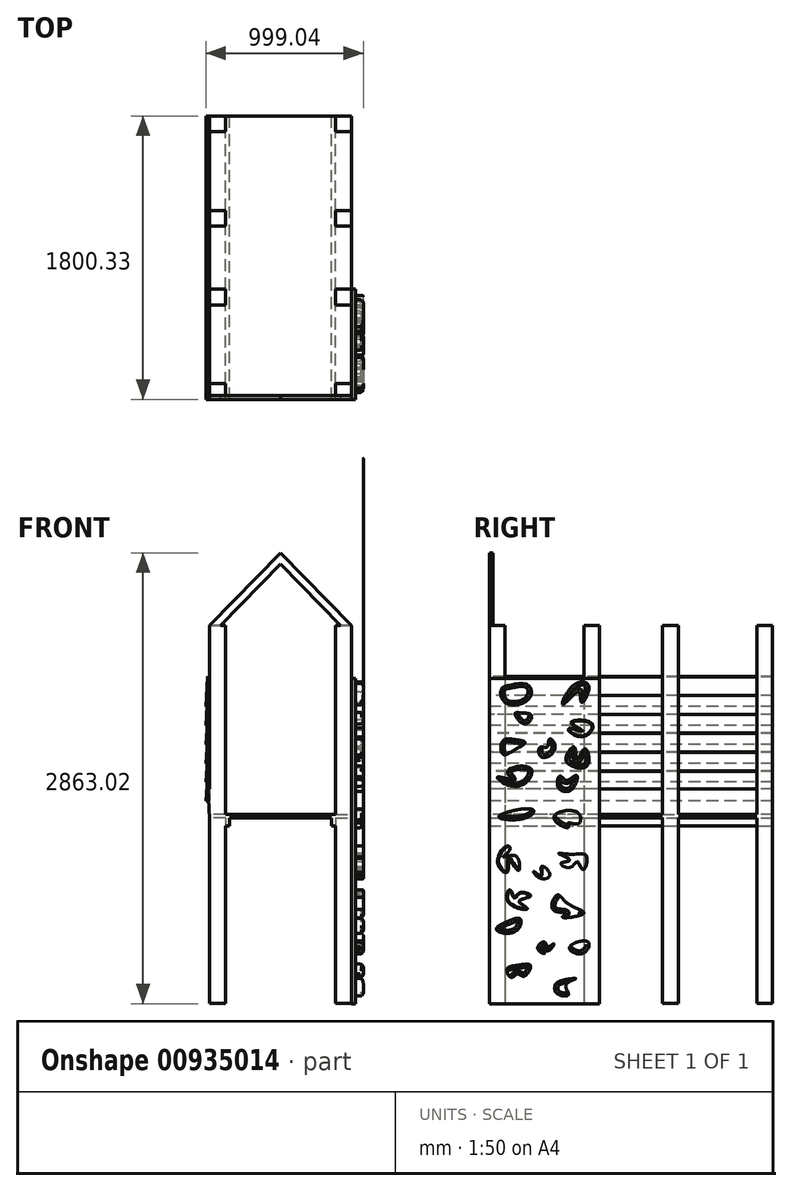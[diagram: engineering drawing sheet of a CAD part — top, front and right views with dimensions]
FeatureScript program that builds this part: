
annotation { "Feature Type Name" : "Feature", "Feature Type Description" : "" }
export const myFeature = defineFeature(function(context is Context, id is Id, definition is map)
    precondition{}
    {
        {
            var Q0;
            Q0=qCreatedBy(makeId("Top.planeOp"),FACE);
            var sketch = newSketch(context, id + "F0", { "sketchPlane" : qUnion([Q0])});
            skLineSegment(sketch, "E0.bottom", {"start": v(450, 900) * mm, "end": v(-450, 900) * mm});
            skLineSegment(sketch, "E0.top", {"start": v(450, -900) * mm, "end": v(-450, -900) * mm});
            skLineSegment(sketch, "E0.left", {"start": v(450, 900) * mm, "end": v(450, -900) * mm});
            skLineSegment(sketch, "E0.right", {"start": v(-450, 900) * mm, "end": v(-450, -900) * mm});
            skPoint(sketch, "E0.middle", {"position": v(0, 0) * mm});
            skSolve(sketch);
        }
        {
            var Q0;
            Q0=makeQuery(id+"F0.imprint","IMPRINT",FACE,{"disambiguationData":[TD([[makeQuery(id+"F0.imprint","IMPRINT",EDGE,{"derivedFrom":sQuery(id+"F0.wireOp",EDGE,"E0.bottom")}),1.0]])]});
            extrude(context, id + "F1", {"entities" : qUnion([Q0]), "depth" : 22 * mm, "offsetDistance" : 25 * mm});
        }
        {
            var Q0;
            Q0=makeQuery(id+"F1.opExtrude","CAP_FACE",FACE,{"disambiguationData":[OSD([sQuery(id+"F0.wireOp",EDGE,"E0.bottom"),sQuery(id+"F0.wireOp",EDGE,"E0.top"),sQuery(id+"F0.wireOp",EDGE,"E0.left"),sQuery(id+"F0.wireOp",EDGE,"E0.right")])],"isStart":false});
            var sketch = newSketch(context, id + "F2", { "sketchPlane" : qUnion([Q0])});
            skLineSegment(sketch, "E1.bottom", {"start": v(-450, 900) * mm, "end": v(-350, 900) * mm});
            skLineSegment(sketch, "E1.top", {"start": v(-450, 800) * mm, "end": v(-350, 800) * mm});
            skLineSegment(sketch, "E1.left", {"start": v(-450, 900) * mm, "end": v(-450, 800) * mm});
            skLineSegment(sketch, "E1.right", {"start": v(-350, 900) * mm, "end": v(-350, 800) * mm});
            skLineSegment(sketch, "E2.bottom", {"start": v(350, 800) * mm, "end": v(450, 800) * mm});
            skLineSegment(sketch, "E2.top", {"start": v(350, 900) * mm, "end": v(450, 900) * mm});
            skLineSegment(sketch, "E2.left", {"start": v(350, 800) * mm, "end": v(350, 900) * mm});
            skLineSegment(sketch, "E2.right", {"start": v(450, 800) * mm, "end": v(450, 900) * mm});
            skLineSegment(sketch, "E3.bottom", {"start": v(-450, -900) * mm, "end": v(-350, -900) * mm});
            skLineSegment(sketch, "E3.top", {"start": v(-450, -800) * mm, "end": v(-350, -800) * mm});
            skLineSegment(sketch, "E3.left", {"start": v(-450, -900) * mm, "end": v(-450, -800) * mm});
            skLineSegment(sketch, "E3.right", {"start": v(-350, -900) * mm, "end": v(-350, -800) * mm});
            skLineSegment(sketch, "E4.bottom", {"start": v(450, -900) * mm, "end": v(350, -900) * mm});
            skLineSegment(sketch, "E4.top", {"start": v(450, -800) * mm, "end": v(350, -800) * mm});
            skLineSegment(sketch, "E4.left", {"start": v(450, -900) * mm, "end": v(450, -800) * mm});
            skLineSegment(sketch, "E4.right", {"start": v(350, -900) * mm, "end": v(350, -800) * mm});
            skLineSegment(sketch, "E5.bottom", {"start": v(350, -300) * mm, "end": v(450, -300) * mm});
            skLineSegment(sketch, "E5.top", {"start": v(350, -200) * mm, "end": v(450, -200) * mm});
            skLineSegment(sketch, "E5.left", {"start": v(350, -300) * mm, "end": v(350, -200) * mm});
            skLineSegment(sketch, "E5.right", {"start": v(450, -300) * mm, "end": v(450, -200) * mm});
            skLineSegment(sketch, "E6.bottom", {"start": v(450, 300) * mm, "end": v(350, 300) * mm});
            skLineSegment(sketch, "E6.top", {"start": v(450, 200) * mm, "end": v(350, 200) * mm});
            skLineSegment(sketch, "E6.left", {"start": v(450, 300) * mm, "end": v(450, 200) * mm});
            skLineSegment(sketch, "E6.right", {"start": v(350, 300) * mm, "end": v(350, 200) * mm});
            skLineSegment(sketch, "E7.bottom", {"start": v(-450, 300) * mm, "end": v(-350, 300) * mm});
            skLineSegment(sketch, "E7.top", {"start": v(-450, 200) * mm, "end": v(-350, 200) * mm});
            skLineSegment(sketch, "E7.left", {"start": v(-450, 300) * mm, "end": v(-450, 200) * mm});
            skLineSegment(sketch, "E7.right", {"start": v(-350, 300) * mm, "end": v(-350, 200) * mm});
            skLineSegment(sketch, "E8.bottom", {"start": v(-450, -300) * mm, "end": v(-350, -300) * mm});
            skLineSegment(sketch, "E8.top", {"start": v(-450, -200) * mm, "end": v(-350, -200) * mm});
            skLineSegment(sketch, "E8.left", {"start": v(-450, -300) * mm, "end": v(-450, -200) * mm});
            skLineSegment(sketch, "E8.right", {"start": v(-350, -300) * mm, "end": v(-350, -200) * mm});
            skSolve(sketch);
        }
        {
            var Q0;
            Q0 = qSketchRegion(id + "F2", true);
            extrude(context, id + "F3", {"entities" : qUnion([Q0]), "operationType" : NewBodyOperationType.ADD, "depth" : 1200 * mm, "offsetDistance" : 25 * mm, "hasSecondDirection" : true, "secondDirectionOppositeDirection" : true, "secondDirectionDepth" : 1200 * mm});
        }
        {
            var Q0;
            Q0=makeQuery(id+"F1.opExtrude","CAP_FACE",FACE,{"disambiguationData":[OSD([sQuery(id+"F0.wireOp",EDGE,"E0.bottom"),sQuery(id+"F0.wireOp",EDGE,"E0.top"),sQuery(id+"F0.wireOp",EDGE,"E0.left"),sQuery(id+"F0.wireOp",EDGE,"E0.right")])],"isStart":true});
            var sketch = newSketch(context, id + "F4", { "sketchPlane" : qUnion([Q0])});
            skLineSegment(sketch, "E9.bottom", {"start": v(-350, 900) * mm, "end": v(-325, 900) * mm});
            skLineSegment(sketch, "E9.top", {"start": v(-350, -900) * mm, "end": v(-325, -900) * mm});
            skLineSegment(sketch, "E9.left", {"start": v(-350, 900) * mm, "end": v(-350, -900) * mm});
            skLineSegment(sketch, "E9.right", {"start": v(-325, 900) * mm, "end": v(-325, -900) * mm});
            skLineSegment(sketch, "E10.bottom", {"start": v(350, 900) * mm, "end": v(325, 900) * mm});
            skLineSegment(sketch, "E10.top", {"start": v(350, -900) * mm, "end": v(325, -900) * mm});
            skLineSegment(sketch, "E10.left", {"start": v(350, 900) * mm, "end": v(350, -900) * mm});
            skLineSegment(sketch, "E10.right", {"start": v(325, 900) * mm, "end": v(325, -900) * mm});
            skSolve(sketch);
        }
        {
            var Q0;
            Q0 = qSketchRegion(id + "F4", true);
            extrude(context, id + "F5", {"entities" : qUnion([Q0]), "operationType" : NewBodyOperationType.ADD, "depth" : 50 * mm, "offsetDistance" : 25 * mm});
        }
        {
            var Q0;
            Q0=makeQuery(id+"F5.boolean.opBoolean","MERGE",FACE,{"derivedFrom":[makeQuery(id+"F3.boolean.opBoolean","MERGE",FACE,{"derivedFrom":[makeQuery(id+"F1.opExtrude","SWEPT_FACE",FACE,{"disambiguationData":[OSD([sQuery(id+"F0.wireOp",EDGE,"E0.top")])]}),makeQuery(id+"F3.opExtrude","SWEPT_FACE",FACE,{"disambiguationData":[OSD([sQuery(id+"F2.wireOp",EDGE,"E3.bottom")])]}),makeQuery(id+"F3.opExtrude","SWEPT_FACE",FACE,{"disambiguationData":[OSD([sQuery(id+"F2.wireOp",EDGE,"E4.bottom")])]})]}),makeQuery(id+"F5.opExtrude","SWEPT_FACE",FACE,{"disambiguationData":[OSD([sQuery(id+"F4.wireOp",EDGE,"E9.bottom")])]}),makeQuery(id+"F5.opExtrude","SWEPT_FACE",FACE,{"disambiguationData":[OSD([sQuery(id+"F4.wireOp",EDGE,"E10.bottom")])]})]});
            var sketch = newSketch(context, id + "F6", { "sketchPlane" : qUnion([Q0])});
            skLineSegment(sketch, "E11", {"start": v(-450, 185.3) * mm, "end": v(-450, -4.7) * mm});
            skLineSegment(sketch, "E12", {"start": v(-450, -4.7) * mm, "end": v(-453, -4.7) * mm});
            skLineSegment(sketch, "E13", {"start": v(-453, -4.7) * mm, "end": v(-462, 184.95) * mm});
            skLineSegment(sketch, "E14", {"start": v(-462, 184.95) * mm, "end": v(-450, 185.3) * mm});
            skSolve(sketch);
        }
        {
            var Q0;
            Q0 = qSketchRegion(id + "F6", true);
            extrude(context, id + "F7", {"entities" : qUnion([Q0]), "operationType" : NewBodyOperationType.ADD, "oppositeDirection" : true, "depth" : 1800 * mm, "offsetDistance" : 25 * mm});
        }
        {
            var Q0;
            Q0=makeQuery(id+"F7.boolean.opBoolean","MERGE",FACE,{"derivedFrom":[makeQuery(id+"F5.boolean.opBoolean","MERGE",FACE,{"derivedFrom":[makeQuery(id+"F3.boolean.opBoolean","MERGE",FACE,{"derivedFrom":[makeQuery(id+"F1.opExtrude","SWEPT_FACE",FACE,{"disambiguationData":[OSD([sQuery(id+"F0.wireOp",EDGE,"E0.top")])]}),makeQuery(id+"F3.opExtrude","SWEPT_FACE",FACE,{"disambiguationData":[OSD([sQuery(id+"F2.wireOp",EDGE,"E3.bottom")])]}),makeQuery(id+"F3.opExtrude","SWEPT_FACE",FACE,{"disambiguationData":[OSD([sQuery(id+"F2.wireOp",EDGE,"E4.bottom")])]})]}),makeQuery(id+"F5.opExtrude","SWEPT_FACE",FACE,{"disambiguationData":[OSD([sQuery(id+"F4.wireOp",EDGE,"E9.bottom")])]}),makeQuery(id+"F5.opExtrude","SWEPT_FACE",FACE,{"disambiguationData":[OSD([sQuery(id+"F4.wireOp",EDGE,"E10.bottom")])]})]}),makeQuery(id+"F7.opExtrude","CAP_FACE",FACE,{"disambiguationData":[OSD([sQuery(id+"F6.wireOp",EDGE,"E11"),sQuery(id+"F6.wireOp",EDGE,"E12"),sQuery(id+"F6.wireOp",EDGE,"E13"),sQuery(id+"F6.wireOp",EDGE,"E14")])],"isStart":true})]});
            var sketch = newSketch(context, id + "F8", { "sketchPlane" : qUnion([Q0])});
            skLineSegment(sketch, "E15", {"start": v(-450, 295.94) * mm, "end": v(-470.4, 107.04) * mm});
            skLineSegment(sketch, "E16", {"start": v(-470.4, 107.04) * mm, "end": v(-473.4, 107.04) * mm});
            skLineSegment(sketch, "E17", {"start": v(-473.4, 107.04) * mm, "end": v(-461.86, 297.77) * mm});
            skLineSegment(sketch, "E18", {"start": v(-461.86, 297.77) * mm, "end": v(-450, 295.94) * mm});
            skLineSegment(sketch, "E19.0.1.0", {"start": v(-470.53, 227.05) * mm, "end": v(-473.53, 227.05) * mm});
            skLineSegment(sketch, "E19.0.1.1", {"start": v(-461.99, 417.78) * mm, "end": v(-450.13, 415.95) * mm});
            skLineSegment(sketch, "E19.0.1.2", {"start": v(-450.13, 415.95) * mm, "end": v(-470.53, 227.05) * mm});
            skLineSegment(sketch, "E19.0.1.3", {"start": v(-473.53, 227.05) * mm, "end": v(-461.99, 417.78) * mm});
            skLineSegment(sketch, "E19.0.2.0", {"start": v(-470.65, 347.06) * mm, "end": v(-473.65, 347.06) * mm});
            skLineSegment(sketch, "E19.0.2.1", {"start": v(-462.12, 537.8) * mm, "end": v(-450.26, 535.96) * mm});
            skLineSegment(sketch, "E19.0.2.2", {"start": v(-450.26, 535.96) * mm, "end": v(-470.65, 347.06) * mm});
            skLineSegment(sketch, "E19.0.2.3", {"start": v(-473.65, 347.06) * mm, "end": v(-462.12, 537.8) * mm});
            skLineSegment(sketch, "E19.0.3.0", {"start": v(-470.78, 467.07) * mm, "end": v(-473.78, 467.07) * mm});
            skLineSegment(sketch, "E19.0.3.1", {"start": v(-462.24, 657.8) * mm, "end": v(-450.38, 655.97) * mm});
            skLineSegment(sketch, "E19.0.3.2", {"start": v(-450.38, 655.97) * mm, "end": v(-470.78, 467.07) * mm});
            skLineSegment(sketch, "E19.0.3.3", {"start": v(-473.78, 467.07) * mm, "end": v(-462.24, 657.8) * mm});
            skLineSegment(sketch, "E19.0.4.0", {"start": v(-470.91, 587.08) * mm, "end": v(-473.91, 587.08) * mm});
            skLineSegment(sketch, "E19.0.4.1", {"start": v(-462.37, 777.81) * mm, "end": v(-450.51, 775.98) * mm});
            skLineSegment(sketch, "E19.0.4.2", {"start": v(-450.51, 775.98) * mm, "end": v(-470.91, 587.08) * mm});
            skLineSegment(sketch, "E19.0.4.3", {"start": v(-473.91, 587.08) * mm, "end": v(-462.37, 777.81) * mm});
            skLineSegment(sketch, "E19.0.5.0", {"start": v(-471.04, 707.1) * mm, "end": v(-474.04, 707.1) * mm});
            skLineSegment(sketch, "E19.0.5.1", {"start": v(-462.5, 897.82) * mm, "end": v(-450.64, 896) * mm});
            skLineSegment(sketch, "E19.0.5.2", {"start": v(-450.64, 896) * mm, "end": v(-471.04, 707.1) * mm});
            skLineSegment(sketch, "E19.0.5.3", {"start": v(-474.04, 707.1) * mm, "end": v(-462.5, 897.82) * mm});
            skLineSegment(sketch, "E19.direction1", {"start": v(-461.86, 297.77) * mm, "end": v(-436.86, 297.77) * mm, "construction": true});
            skLineSegment(sketch, "E19.direction2", {"start": v(-461.86, 297.77) * mm, "end": v(-461.99, 417.78) * mm, "construction": true});
            skSolve(sketch);
        }
        {
            var Q0;
            Q0=makeQuery(id+"F8.imprint","IMPRINT",FACE,{"disambiguationData":[TD([[makeQuery(id+"F8.imprint","IMPRINT",EDGE,{"derivedFrom":sQuery(id+"F8.wireOp",EDGE,"E19.0.1.0")}),-1.0]])]});
            var Q1;
            Q1=makeQuery(id+"F8.imprint","IMPRINT",FACE,{"disambiguationData":[TD([[makeQuery(id+"F8.imprint","IMPRINT",EDGE,{"derivedFrom":sQuery(id+"F8.wireOp",EDGE,"E19.0.2.0")}),-1.0]])]});
            var Q2;
            Q2=makeQuery(id+"F8.imprint","IMPRINT",FACE,{"disambiguationData":[TD([[makeQuery(id+"F8.imprint","IMPRINT",EDGE,{"derivedFrom":sQuery(id+"F8.wireOp",EDGE,"E19.0.3.0")}),-1.0]])]});
            var Q3;
            Q3=makeQuery(id+"F8.imprint","IMPRINT",FACE,{"disambiguationData":[TD([[makeQuery(id+"F8.imprint","IMPRINT",EDGE,{"derivedFrom":sQuery(id+"F8.wireOp",EDGE,"E19.0.4.0")}),-1.0]])]});
            var Q4;
            Q4=makeQuery(id+"F8.imprint","IMPRINT",FACE,{"disambiguationData":[TD([[makeQuery(id+"F8.imprint","IMPRINT",EDGE,{"derivedFrom":sQuery(id+"F8.wireOp",EDGE,"E19.0.5.0")}),-1.0]])]});
            extrude(context, id + "F9", {"entities" : qUnion([Q0, Q1, Q2, Q3, Q4]), "oppositeDirection" : true, "depth" : 1800 * mm, "offsetDistance" : 25 * mm});
        }
        {
            var Q0;
            {var subQ0=sQuery(id+"F8.wireOp",EDGE,"E16");Q0=makeQuery(id+"F8.imprint","IMPRINT",FACE,{"disambiguationData":[TD([[makeQuery(id+"F8.imprint","IMPRINT",EDGE,{"derivedFrom":subQ0}),-1.0]])]});}
            extrude(context, id + "F10", {"entities" : qUnion([Q0]), "oppositeDirection" : true, "depth" : 1800 * mm, "offsetDistance" : 25 * mm});
        }
        {
            var Q0;
            Q0=makeQuery(id+"F7.boolean.opBoolean","MERGE",FACE,{"derivedFrom":[makeQuery(id+"F5.boolean.opBoolean","MERGE",FACE,{"derivedFrom":[makeQuery(id+"F3.boolean.opBoolean","MERGE",FACE,{"derivedFrom":[makeQuery(id+"F1.opExtrude","SWEPT_FACE",FACE,{"disambiguationData":[OSD([sQuery(id+"F0.wireOp",EDGE,"E0.bottom")])]}),makeQuery(id+"F3.opExtrude","SWEPT_FACE",FACE,{"disambiguationData":[OSD([sQuery(id+"F2.wireOp",EDGE,"E1.bottom")])]}),makeQuery(id+"F3.opExtrude","SWEPT_FACE",FACE,{"disambiguationData":[OSD([sQuery(id+"F2.wireOp",EDGE,"E2.top")])]})]}),makeQuery(id+"F5.opExtrude","SWEPT_FACE",FACE,{"disambiguationData":[OSD([sQuery(id+"F4.wireOp",EDGE,"E9.top")])]}),makeQuery(id+"F5.opExtrude","SWEPT_FACE",FACE,{"disambiguationData":[OSD([sQuery(id+"F4.wireOp",EDGE,"E10.top")])]})]}),makeQuery(id+"F7.opExtrude","CAP_FACE",FACE,{"disambiguationData":[OSD([sQuery(id+"F6.wireOp",EDGE,"E11"),sQuery(id+"F6.wireOp",EDGE,"E12"),sQuery(id+"F6.wireOp",EDGE,"E13"),sQuery(id+"F6.wireOp",EDGE,"E14")])],"isStart":false})]});
            cPlane(context, id + "F11", {"entities" : qUnion([Q0]), "cplaneType" : CPlaneType.OFFSET, "offset" : 300 * mm, "oppositeDirection" : true, "width" : 150 * mm, "height" : 150 * mm});
        }
        {
            var Q0;
            Q0=qCreatedBy(id+"F11.planeOp",FACE);
            var sketch = newSketch(context, id + "F12", { "sketchPlane" : qUnion([Q0])});
            skFitSpline(sketch, "E20", {"points": [v(-446.84, 20.94) * mm, v(-1018.85, -218.36) * mm, v(-1616.22, -815.28) * mm, v(-2211.53, -1175.8) * mm], "startDerivative": vector(-3689.56, -4.26) * mm, "endDerivative": vector(-1535.93, 0) * mm});
            skLineSegment(sketch, "E21", {"start": v(-448.7, -1175.8) * mm, "end": v(-2388.55, -1175.8) * mm, "construction": true});
            skSolve(sketch);
        }
        {
            var Q0;
            Q0=makeQuery(id+"F3.boolean.opBoolean","MERGE",FACE,{"derivedFrom":[makeQuery(id+"F1.opExtrude","SWEPT_FACE",FACE,{"disambiguationData":[OSD([sQuery(id+"F0.wireOp",EDGE,"E0.left")])]}),makeQuery(id+"F3.opExtrude","SWEPT_FACE",FACE,{"disambiguationData":[OSD([sQuery(id+"F2.wireOp",EDGE,"E2.right")])]}),makeQuery(id+"F3.opExtrude","SWEPT_FACE",FACE,{"disambiguationData":[OSD([sQuery(id+"F2.wireOp",EDGE,"E4.left")])]}),makeQuery(id+"F3.opExtrude","SWEPT_FACE",FACE,{"disambiguationData":[OSD([sQuery(id+"F2.wireOp",EDGE,"E5.right")])]}),makeQuery(id+"F3.opExtrude","SWEPT_FACE",FACE,{"disambiguationData":[OSD([sQuery(id+"F2.wireOp",EDGE,"E6.left")])]})]});
            var sketch = newSketch(context, id + "F13", { "sketchPlane" : qUnion([Q0])});
            skLineSegment(sketch, "E22.bottom", {"start": v(300, 70.69) * mm, "end": v(332.87, 70.69) * mm});
            skLineSegment(sketch, "E22.top", {"start": v(300, 0) * mm, "end": v(800, 0) * mm});
            skLineSegment(sketch, "E22.left", {"start": v(300, 70.69) * mm, "end": v(300, 0) * mm});
            skLineSegment(sketch, "E22.right", {"start": v(800, 70.69) * mm, "end": v(800, 0) * mm});
            skLineSegment(sketch, "E23.top", {"start": v(332.87, 22) * mm, "end": v(769.2, 22) * mm});
            skLineSegment(sketch, "E23.left", {"start": v(332.87, 70.69) * mm, "end": v(332.87, 22) * mm});
            skLineSegment(sketch, "E23.right", {"start": v(769.2, 70.69) * mm, "end": v(769.2, 22) * mm});
            skLineSegment(sketch, "E24.trimOffspring", {"start": v(769.2, 70.69) * mm, "end": v(800, 70.69) * mm});
            skSolve(sketch);
        }
        {
            var Q0;
            Q0 = qSketchRegion(id + "F13", true);
            var Q1;
            Q1 = qBodyType(qCreatedBy(id + "F13" ,EDGE), BodyType.WIRE);
            var Q2;
            Q2 = qBodyType(qCreatedBy(id + "F12" ,EDGE), BodyType.WIRE);
            sweep(context, id + "F14", {"bodyType" : ToolBodyType.SURFACE, "operationType" : NewBodyOperationType.ADD, "profiles" : qUnion([Q0]), "surfaceProfiles" : qUnion([Q1]), "path" : qUnion([Q2]), "keepProfileOrientation" : true});
        }
        {
            var Q0;
            {var subQ3=sQuery(id+"F2.wireOp",EDGE,"E4.left");Q0=makeQuery(id+"F13.imprint","IMPRINT",FACE,{"disambiguationData":[TD([[makeQuery(id+"F13.imprint","IMPRINT",EDGE,{"derivedFrom":makeQuery(id+"F3.opExtrude","CAP_EDGE",EDGE,{"disambiguationData":[OSD([subQ3])],"isStart":true})}),-1.0]])]});}
            var sketch = newSketch(context, id + "F15", { "sketchPlane" : qUnion([Q0])});
            skLineSegment(sketch, "E25.bottom", {"start": v(-900.33, -1180.28) * mm, "end": v(-198.92, -1180.28) * mm});
            skLineSegment(sketch, "E25.top", {"start": v(-900.33, 886.65) * mm, "end": v(-198.92, 886.65) * mm});
            skLineSegment(sketch, "E25.left", {"start": v(-900.33, -1180.28) * mm, "end": v(-900.33, 886.65) * mm});
            skLineSegment(sketch, "E25.right", {"start": v(-198.92, -1180.28) * mm, "end": v(-198.92, 886.65) * mm});
            skSolve(sketch);
        }
        {
            var Q0;
            Q0 = qSketchRegion(id + "F15", true);
            extrude(context, id + "F16", {"entities" : qUnion([Q0]), "operationType" : NewBodyOperationType.ADD, "depth" : 25 * mm, "offsetDistance" : 25 * mm});
        }
        {
            var Q0;
            Q0=makeQuery(id+"F16.opExtrude","CAP_FACE",FACE,{"disambiguationData":[OSD([sQuery(id+"F15.wireOp",EDGE,"E25.bottom"),sQuery(id+"F15.wireOp",EDGE,"E25.top"),sQuery(id+"F15.wireOp",EDGE,"E25.left"),sQuery(id+"F15.wireOp",EDGE,"E25.right")])],"isStart":false});
            var sketch = newSketch(context, id + "F17", { "sketchPlane" : qUnion([Q0])});
            skFitSpline(sketch, "E26", {"points": [v(-761.33, -1013.23) * mm, v(-786.6, -960.93) * mm, v(-722.98, -937.4) * mm, v(-638.43, -939.14) * mm, v(-680.27, -1006.25) * mm, v(-718.62, -992.3) * mm, v(-761.33, -1013.23) * mm]});
            skFitSpline(sketch, "E27", {"points": [v(-483.3, -1070.75) * mm, v(-443.2, -1035.02) * mm, v(-350.8, -1021.94) * mm, v(-413.56, -1062.04) * mm, v(-397, -1123.05) * mm, v(-464.99, -1119.56) * mm, v(-483.3, -1070.75) * mm]});
            skFitSpline(sketch, "E28", {"points": [v(-296.77, -781.38) * mm, v(-390.9, -825.83) * mm, v(-316.81, -863.31) * mm, v(-265.4, -805.79) * mm, v(-296.77, -781.38) * mm]});
            skFitSpline(sketch, "E29", {"points": [v(-549.53, -789.23) * mm, v(-592.24, -830.2) * mm, v(-548.66, -860.7) * mm, v(-558.25, -840.65) * mm, v(-524.26, -843.26) * mm, v(-491.13, -799.68) * mm, v(-526, -818.86) * mm, v(-549.53, -789.23) * mm]});
            skFitSpline(sketch, "E30", {"points": [v(-786.6, -659.36) * mm, v(-702.06, -643.67) * mm, v(-739.54, -723.86) * mm, v(-854.6, -709.9) * mm, v(-786.6, -659.36) * mm]});
            skFitSpline(sketch, "E31", {"points": [v(-402.23, -544.3) * mm, v(-300.25, -607.06) * mm, v(-434.48, -630.6) * mm, v(-413.56, -607.06) * mm, v(-495.5, -582.66) * mm, v(-469.34, -491.14) * mm, v(-402.23, -544.3) * mm]});
            skFitSpline(sketch, "E32", {"points": [v(-707.3, -475.45) * mm, v(-638.43, -496.37) * mm, v(-709.9, -529.49) * mm, v(-658.48, -577.43) * mm, v(-779.63, -534.72) * mm, v(-768.3, -458.02) * mm, v(-740.41, -505.08) * mm, v(-707.3, -475.45) * mm]});
            skFitSpline(sketch, "E33", {"points": [v(-377.2, -231.25) * mm, v(-282.72, -244.4) * mm, v(-303.26, -329.02) * mm, v(-341.88, -278.08) * mm, v(-384.6, -315.05) * mm, v(-445.4, -291.23) * mm, v(-389.53, -268.22) * mm, v(-456.9, -227.14) * mm, v(-377.2, -231.25) * mm]});
            skFitSpline(sketch, "E34", {"points": [v(-778.15, -177.02) * mm, v(-847.17, -280.55) * mm, v(-784.73, -342.99) * mm, v(-776.51, -256.72) * mm, v(-716.53, -334.77) * mm, v(-717.35, -259.19) * mm, v(-765.83, -240.29) * mm, v(-812.66, -246.86) * mm, v(-772.4, -208.25) * mm, v(-778.15, -177.02) * mm]});
            skFitSpline(sketch, "E35", {"points": [v(-567, -308.48) * mm, v(-515.24, -361.89) * mm, v(-580.15, -382.43) * mm, v(-617.94, -341.35) * mm, v(-572.75, -366.82) * mm, v(-567, -308.48) * mm]});
            skFitSpline(sketch, "E36", {"points": [v(-344.18, 36.5) * mm, v(-489.76, 0) * mm, v(-398.77, -61.1) * mm, v(-400.43, -34.63) * mm, v(-333.42, -36.29) * mm, v(-344.18, 36.5) * mm]});
            skFitSpline(sketch, "E37", {"points": [v(-838.01, 10.04) * mm, v(-624.6, 53.05) * mm, v(-669.27, 0) * mm, v(-838.01, 10.04) * mm]});
            skFitSpline(sketch, "E38", {"points": [v(-345.16, 269.49) * mm, v(-411.16, 238.1) * mm, v(-449.8, 265.46) * mm, v(-464.28, 198.65) * mm, v(-378.96, 177.72) * mm, v(-345.16, 269.49) * mm]});
            skFitSpline(sketch, "E39", {"points": [v(-783.03, 294.44) * mm, v(-637.34, 313.76) * mm, v(-723.47, 200.26) * mm, v(-846.62, 259.02) * mm, v(-757.28, 245.34) * mm, v(-783.03, 294.44) * mm]});
            skFitSpline(sketch, "E40", {"points": [v(-736.45, 661.19) * mm, v(-675.57, 597.02) * mm, v(-631.15, 648.85) * mm, v(-700.25, 666.95) * mm, v(-736.45, 661.19) * mm]});
            skFitSpline(sketch, "E41", {"points": [v(-361.3, 844.65) * mm, v(-268.34, 833.13) * mm, v(-314.4, 733.58) * mm, v(-330.86, 800.22) * mm, v(-432.05, 720.42) * mm, v(-361.3, 844.65) * mm]});
            skFitSpline(sketch, "E42", {"points": [v(-384.34, 604.42) * mm, v(-246.12, 597.84) * mm, v(-316.87, 513.92) * mm, v(-399.14, 569.87) * mm, v(-308.65, 554.24) * mm, v(-384.34, 604.42) * mm]});
            skFitSpline(sketch, "E43", {"points": [v(-746.32, 498.3) * mm, v(-673.1, 479.37) * mm, v(-747.15, 427.54) * mm, v(-808.85, 402.04) * mm, v(-826.13, 462.1) * mm, v(-795.69, 499.94) * mm, v(-746.32, 498.3) * mm]});
            skFitSpline(sketch, "E44", {"points": [v(-516.8, 501.58) * mm, v(-482.24, 443.17) * mm, v(-566.98, 385.58) * mm, v(-579.32, 446.46) * mm, v(-532.42, 451.4) * mm, v(-516.8, 501.58) * mm]});
            skFitSpline(sketch, "E45", {"points": [v(-294.66, 438.23) * mm, v(-276.56, 333.75) * mm, v(-400.8, 346.1) * mm, v(-403.26, 405.33) * mm, v(-359.66, 449.75) * mm, v(-342.38, 365.84) * mm, v(-294.66, 438.23) * mm]});
            skFitSpline(sketch, "E46", {"points": [v(-758.66, 845.47) * mm, v(-650.07, 841.36) * mm, v(-649.25, 754.97) * mm, v(-796.5, 731.12) * mm, v(-822.84, 815.03) * mm, v(-758.66, 845.47) * mm]});
            skSolve(sketch);
        }
        {
            var Q0;
            Q0 = qSketchRegion(id + "F17", true);
            extrude(context, id + "F18", {"entities" : qUnion([Q0]), "operationType" : NewBodyOperationType.ADD, "depth" : 50 * mm, "offsetDistance" : 25 * mm});
        }
        {
            var Q0;
            Q0=makeQuery(id+"F18.opExtrude","CAP_FACE",FACE,{"disambiguationData":[OSD([sQuery(id+"F17.wireOp",EDGE,"E27")])],"isStart":false});
            var Q1;
            Q1=makeQuery(id+"F18.opExtrude","CAP_FACE",FACE,{"disambiguationData":[OSD([sQuery(id+"F17.wireOp",EDGE,"E28")])],"isStart":false});
            var Q2;
            Q2=makeQuery(id+"F18.opExtrude","CAP_FACE",FACE,{"disambiguationData":[OSD([sQuery(id+"F17.wireOp",EDGE,"E26")])],"isStart":false});
            var Q3;
            Q3=makeQuery(id+"F18.opExtrude","CAP_FACE",FACE,{"disambiguationData":[OSD([sQuery(id+"F17.wireOp",EDGE,"E30")])],"isStart":false});
            var Q4;
            Q4=makeQuery(id+"F18.opExtrude","CAP_FACE",FACE,{"disambiguationData":[OSD([sQuery(id+"F17.wireOp",EDGE,"E29")])],"isStart":false});
            var Q5;
            Q5=makeQuery(id+"F18.opExtrude","CAP_FACE",FACE,{"disambiguationData":[OSD([sQuery(id+"F17.wireOp",EDGE,"E31")])],"isStart":false});
            fillet(context, id + "F19", {"entities" : qUnion([Q0, Q1, Q2, Q3, Q4, Q5]), "radius" : 20 * mm, "tangentPropagation" : true, "allowEdgeOverflow" : false});
        }
        {
            var Q0;
            Q0=makeQuery(id+"F18.opExtrude","CAP_FACE",FACE,{"disambiguationData":[OSD([sQuery(id+"F17.wireOp",EDGE,"E36")])],"isStart":false});
            var Q1;
            Q1=makeQuery(id+"F18.opExtrude","CAP_FACE",FACE,{"disambiguationData":[OSD([sQuery(id+"F17.wireOp",EDGE,"E37")])],"isStart":false});
            var Q2;
            Q2=makeQuery(id+"F18.opExtrude","CAP_FACE",FACE,{"disambiguationData":[OSD([sQuery(id+"F17.wireOp",EDGE,"E38")])],"isStart":false});
            var Q3;
            Q3=makeQuery(id+"F18.opExtrude","CAP_FACE",FACE,{"disambiguationData":[OSD([sQuery(id+"F17.wireOp",EDGE,"E39")])],"isStart":false});
            var Q4;
            Q4=makeQuery(id+"F18.opExtrude","CAP_FACE",FACE,{"disambiguationData":[OSD([sQuery(id+"F17.wireOp",EDGE,"E45")])],"isStart":false});
            var Q5;
            Q5=makeQuery(id+"F18.opExtrude","CAP_FACE",FACE,{"disambiguationData":[OSD([sQuery(id+"F17.wireOp",EDGE,"E44")])],"isStart":false});
            var Q6;
            Q6=makeQuery(id+"F18.opExtrude","CAP_FACE",FACE,{"disambiguationData":[OSD([sQuery(id+"F17.wireOp",EDGE,"E43")])],"isStart":false});
            var Q7;
            Q7=makeQuery(id+"F18.opExtrude","CAP_FACE",FACE,{"disambiguationData":[OSD([sQuery(id+"F17.wireOp",EDGE,"E40")])],"isStart":false});
            var Q8;
            Q8=makeQuery(id+"F18.opExtrude","CAP_FACE",FACE,{"disambiguationData":[OSD([sQuery(id+"F17.wireOp",EDGE,"E46")])],"isStart":false});
            var Q9;
            Q9=makeQuery(id+"F18.opExtrude","CAP_FACE",FACE,{"disambiguationData":[OSD([sQuery(id+"F17.wireOp",EDGE,"E41")])],"isStart":false});
            fillet(context, id + "F20", {"entities" : qUnion([Q0, Q1, Q2, Q3, Q4, Q5, Q6, Q7, Q8, Q9]), "radius" : 20 * mm, "tangentPropagation" : true, "allowEdgeOverflow" : false});
        }
        {
            var Q0;
            Q0=makeQuery(id+"F18.opExtrude","CAP_FACE",FACE,{"disambiguationData":[OSD([sQuery(id+"F17.wireOp",EDGE,"E32")])],"isStart":false});
            var Q1;
            Q1=makeQuery(id+"F18.opExtrude","CAP_FACE",FACE,{"disambiguationData":[OSD([sQuery(id+"F17.wireOp",EDGE,"E35")])],"isStart":false});
            var Q2;
            Q2=makeQuery(id+"F18.opExtrude","CAP_FACE",FACE,{"disambiguationData":[OSD([sQuery(id+"F17.wireOp",EDGE,"E34")])],"isStart":false});
            var Q3;
            Q3=makeQuery(id+"F18.opExtrude","CAP_FACE",FACE,{"disambiguationData":[OSD([sQuery(id+"F17.wireOp",EDGE,"E33")])],"isStart":false});
            var Q4;
            Q4=makeQuery(id+"F18.opExtrude","CAP_FACE",FACE,{"disambiguationData":[OSD([sQuery(id+"F17.wireOp",EDGE,"E42")])],"isStart":false});
            fillet(context, id + "F21", {"entities" : qUnion([Q0, Q1, Q2, Q3, Q4]), "radius" : 5 * mm, "tangentPropagation" : true, "allowEdgeOverflow" : false});
        }
        {
            var Q0;
            Q0=makeQuery(id+"F7.boolean.opBoolean","MERGE",FACE,{"derivedFrom":[makeQuery(id+"F5.boolean.opBoolean","MERGE",FACE,{"derivedFrom":[makeQuery(id+"F3.boolean.opBoolean","MERGE",FACE,{"derivedFrom":[makeQuery(id+"F1.opExtrude","SWEPT_FACE",FACE,{"disambiguationData":[OSD([sQuery(id+"F0.wireOp",EDGE,"E0.top")])]}),makeQuery(id+"F3.opExtrude","SWEPT_FACE",FACE,{"disambiguationData":[OSD([sQuery(id+"F2.wireOp",EDGE,"E3.bottom")])]}),makeQuery(id+"F3.opExtrude","SWEPT_FACE",FACE,{"disambiguationData":[OSD([sQuery(id+"F2.wireOp",EDGE,"E4.bottom")])]})]}),makeQuery(id+"F5.opExtrude","SWEPT_FACE",FACE,{"disambiguationData":[OSD([sQuery(id+"F4.wireOp",EDGE,"E9.bottom")])]}),makeQuery(id+"F5.opExtrude","SWEPT_FACE",FACE,{"disambiguationData":[OSD([sQuery(id+"F4.wireOp",EDGE,"E10.bottom")])]})]}),makeQuery(id+"F7.opExtrude","CAP_FACE",FACE,{"disambiguationData":[OSD([sQuery(id+"F6.wireOp",EDGE,"E11"),sQuery(id+"F6.wireOp",EDGE,"E12"),sQuery(id+"F6.wireOp",EDGE,"E13"),sQuery(id+"F6.wireOp",EDGE,"E14")])],"isStart":true})]});
            var sketch = newSketch(context, id + "F22", { "sketchPlane" : qUnion([Q0])});
            skLineSegment(sketch, "E47", {"start": v(-450, 1222) * mm, "end": v(0, 1682.74) * mm});
            skLineSegment(sketch, "E48", {"start": v(0, 1682.74) * mm, "end": v(450, 1222) * mm});
            skLineSegment(sketch, "E49.0", {"start": v(0, 1611.18) * mm, "end": v(414.23, 1187.06) * mm});
            skLineSegment(sketch, "E49.1", {"start": v(-414.23, 1187.06) * mm, "end": v(0, 1611.18) * mm});
            skLineSegment(sketch, "E50", {"start": v(-450, 1222) * mm, "end": v(-414.23, 1187.06) * mm});
            skLineSegment(sketch, "E51", {"start": v(414.23, 1187.06) * mm, "end": v(450, 1222) * mm});
            skSolve(sketch);
        }
        {
            var Q0;
            Q0 = qSketchRegion(id + "F22", true);
            extrude(context, id + "F23", {"entities" : qUnion([Q0]), "operationType" : NewBodyOperationType.ADD, "oppositeDirection" : true, "depth" : 25 * mm, "offsetDistance" : 25 * mm});
        }
    });
